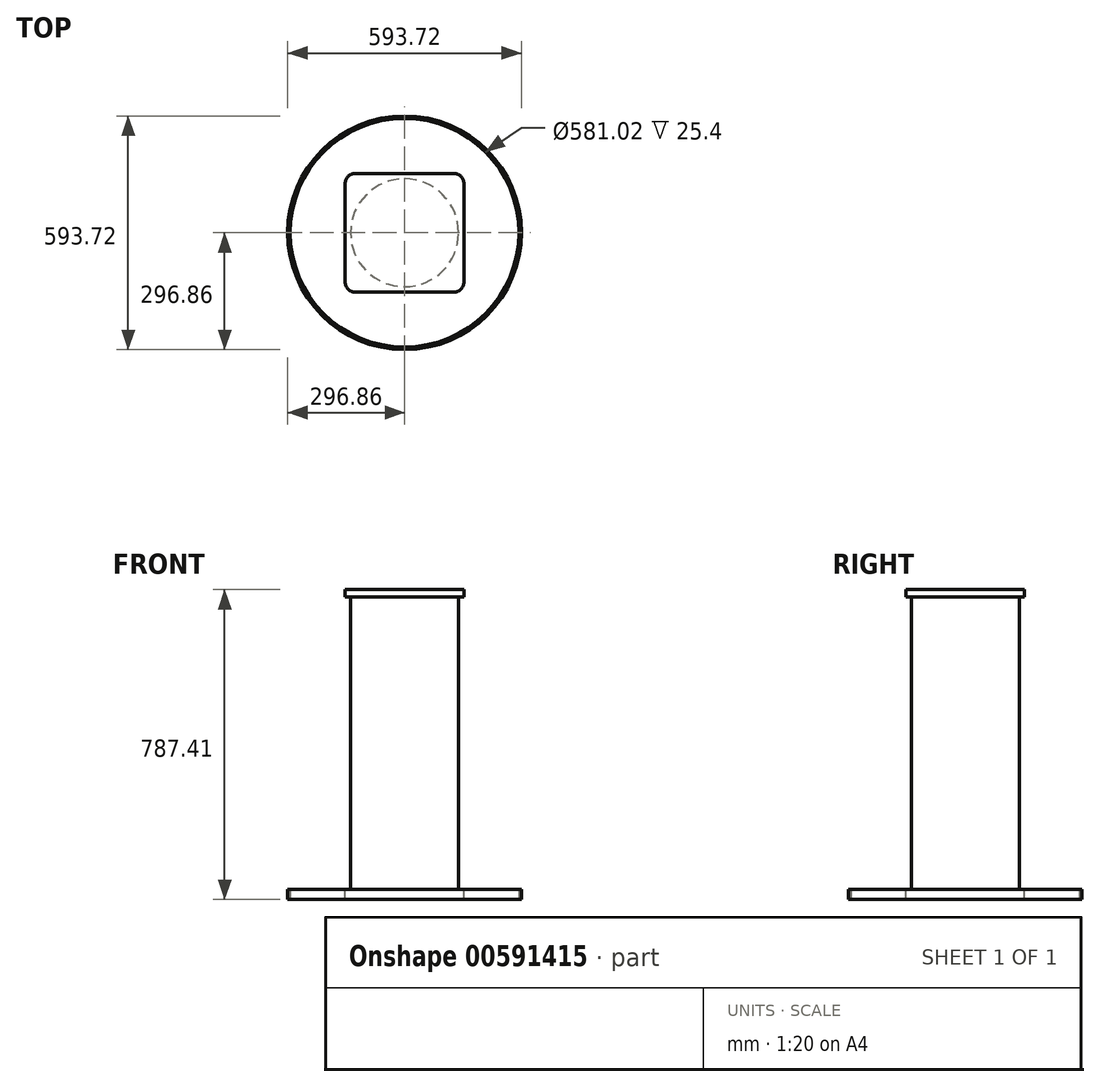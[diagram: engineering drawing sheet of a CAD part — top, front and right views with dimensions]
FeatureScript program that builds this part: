
annotation { "Feature Type Name" : "Feature", "Feature Type Description" : "" }
export const myFeature = defineFeature(function(context is Context, id is Id, definition is map)
    precondition{}
    {
        {
            var Q0;
            Q0=qCreatedBy(makeId("Top.planeOp"),FACE);
            var sketch = newSketch(context, id + "F0", { "sketchPlane" : qUnion([Q0])});
            skCircle(sketch, "E0", {"center": v(0, 0) * mm, "radius": 137.16 * mm});
            skSolve(sketch);
        }
        {
            var Q0;
            Q0 = qSketchRegion(id + "F0", true);
            extrude(context, id + "F1", {"entities" : qUnion([Q0]), "depth" : 742.95 * mm, "offsetDistance" : 25.4 * mm, "symmetric" : true});
        }
        {
            var Q0;
            Q0=makeQuery(id+"F1.opExtrude","CAP_FACE",FACE,{"disambiguationData":[OSD([sQuery(id+"F0.wireOp",EDGE,"E0")])],"isStart":false});
            var sketch = newSketch(context, id + "F2", { "sketchPlane" : qUnion([Q0])});
            skLineSegment(sketch, "E1.bottom", {"start": v(150.81, -150.81) * mm, "end": v(-150.81, -150.81) * mm});
            skLineSegment(sketch, "E1.top", {"start": v(150.81, 150.81) * mm, "end": v(-150.81, 150.81) * mm});
            skLineSegment(sketch, "E1.left", {"start": v(150.81, -150.81) * mm, "end": v(150.81, 150.81) * mm});
            skLineSegment(sketch, "E1.right", {"start": v(-150.81, -150.81) * mm, "end": v(-150.81, 150.81) * mm});
            skPoint(sketch, "E1.middle", {"position": v(0, 0) * mm});
            skSolve(sketch);
        }
        {
            var Q0;
            Q0 = qSketchRegion(id + "F2", true);
            extrude(context, id + "F3", {"entities" : qUnion([Q0]), "operationType" : NewBodyOperationType.ADD, "depth" : 19.05 * mm, "offsetDistance" : 25.4 * mm});
        }
        {
            var Q0;
            Q0=makeQuery(id+"F1.opExtrude","CAP_FACE",FACE,{"disambiguationData":[OSD([sQuery(id+"F0.wireOp",EDGE,"E0")])],"isStart":true});
            var sketch = newSketch(context, id + "F4", { "sketchPlane" : qUnion([Q0])});
            skLineSegment(sketch, "E2.0.0", {"start": v(150.81, 150.81) * mm, "end": v(150.81, -150.81) * mm});
            skLineSegment(sketch, "E2.0.1", {"start": v(150.81, -150.81) * mm, "end": v(-150.81, -150.81) * mm});
            skLineSegment(sketch, "E2.0.2", {"start": v(-150.81, -150.81) * mm, "end": v(-150.81, 150.81) * mm});
            skLineSegment(sketch, "E2.0.3", {"start": v(-150.81, 150.81) * mm, "end": v(150.81, 150.81) * mm});
            skCircle(sketch, "E3.0", {"center": v(0, 0) * mm, "radius": 137.16 * mm, "construction": true});
            skPoint(sketch, "E4", {"position": v(0, 137.16) * mm});
            skSolve(sketch);
        }
        {
            var Q0;
            Q0 = qSketchRegion(id + "F4", true);
            extrude(context, id + "F5", {"entities" : qUnion([Q0]), "operationType" : NewBodyOperationType.ADD, "depth" : 25.4 * mm, "offsetDistance" : 25.4 * mm});
        }
        {
            var Q0;
            Q0=makeQuery(id+"F5.opExtrude","SWEPT_EDGE",EDGE,{"disambiguationData":[OSD([sQuery(id+"F4.wireOp",EDGE,"E2.0.0"),sQuery(id+"F4.wireOp",EDGE,"E2.0.3")])]});
            var Q1;
            Q1=makeQuery(id+"F5.opExtrude","SWEPT_EDGE",EDGE,{"disambiguationData":[OSD([sQuery(id+"F4.wireOp",EDGE,"E2.0.2"),sQuery(id+"F4.wireOp",EDGE,"E2.0.3")])]});
            var Q2;
            Q2=makeQuery(id+"F5.opExtrude","SWEPT_EDGE",EDGE,{"disambiguationData":[OSD([sQuery(id+"F4.wireOp",EDGE,"E2.0.0"),sQuery(id+"F4.wireOp",EDGE,"E2.0.1")])]});
            var Q3;
            Q3=makeQuery(id+"F5.opExtrude","SWEPT_EDGE",EDGE,{"disambiguationData":[OSD([sQuery(id+"F4.wireOp",EDGE,"E2.0.1"),sQuery(id+"F4.wireOp",EDGE,"E2.0.2")])]});
            var Q4;
            Q4=makeQuery(id+"F3.opExtrude","SWEPT_EDGE",EDGE,{"disambiguationData":[OSD([sQuery(id+"F2.wireOp",EDGE,"E1.top"),sQuery(id+"F2.wireOp",EDGE,"E1.right")])]});
            var Q5;
            Q5=makeQuery(id+"F3.opExtrude","SWEPT_EDGE",EDGE,{"disambiguationData":[OSD([sQuery(id+"F2.wireOp",EDGE,"E1.top"),sQuery(id+"F2.wireOp",EDGE,"E1.left")])]});
            var Q6;
            Q6=makeQuery(id+"F3.opExtrude","SWEPT_EDGE",EDGE,{"disambiguationData":[OSD([sQuery(id+"F2.wireOp",EDGE,"E1.bottom"),sQuery(id+"F2.wireOp",EDGE,"E1.right")])]});
            var Q7;
            Q7=makeQuery(id+"F3.opExtrude","SWEPT_EDGE",EDGE,{"disambiguationData":[OSD([sQuery(id+"F2.wireOp",EDGE,"E1.bottom"),sQuery(id+"F2.wireOp",EDGE,"E1.left")])]});
            fillet(context, id + "F6", {"entities" : qUnion([Q0, Q1, Q2, Q3, Q4, Q5, Q6, Q7]), "radius" : 25.4 * mm, "tangentPropagation" : true, "allowEdgeOverflow" : false});
        }
        {
            var Q0;
            Q0=makeQuery(id+"F5.opExtrude","CAP_FACE",FACE,{"disambiguationData":[OSD([sQuery(id+"F4.wireOp",EDGE,"E2.0.0"),sQuery(id+"F4.wireOp",EDGE,"E2.0.1"),sQuery(id+"F4.wireOp",EDGE,"E2.0.2"),sQuery(id+"F4.wireOp",EDGE,"E2.0.3")])],"isStart":false});
            var sketch = newSketch(context, id + "F7", { "sketchPlane" : qUnion([Q0])});
            skLineSegment(sketch, "E5.bottom", {"start": v(290.51, -290.51) * mm, "end": v(-290.51, -290.51) * mm, "construction": true});
            skLineSegment(sketch, "E5.top", {"start": v(290.51, 290.51) * mm, "end": v(-290.51, 290.51) * mm, "construction": true});
            skLineSegment(sketch, "E5.left", {"start": v(290.51, -290.51) * mm, "end": v(290.51, 290.51) * mm, "construction": true});
            skLineSegment(sketch, "E5.right", {"start": v(-290.51, -290.51) * mm, "end": v(-290.51, 290.51) * mm, "construction": true});
            skPoint(sketch, "E5.middle", {"position": v(0, 0) * mm});
            skCircle(sketch, "E6", {"center": v(0, 0) * mm, "radius": 290.51 * mm});
            skCircle(sketch, "E7.0", {"center": v(0, 0) * mm, "radius": 296.86 * mm});
            skSolve(sketch);
        }
        {
            var Q0;
            Q0 = qSketchRegion(id + "F7", true);
            extrude(context, id + "F8", {"entities" : qUnion([Q0]), "operationType" : NewBodyOperationType.ADD, "oppositeDirection" : true, "depth" : 25.4 * mm, "offsetDistance" : 25.4 * mm});
        }
    });
